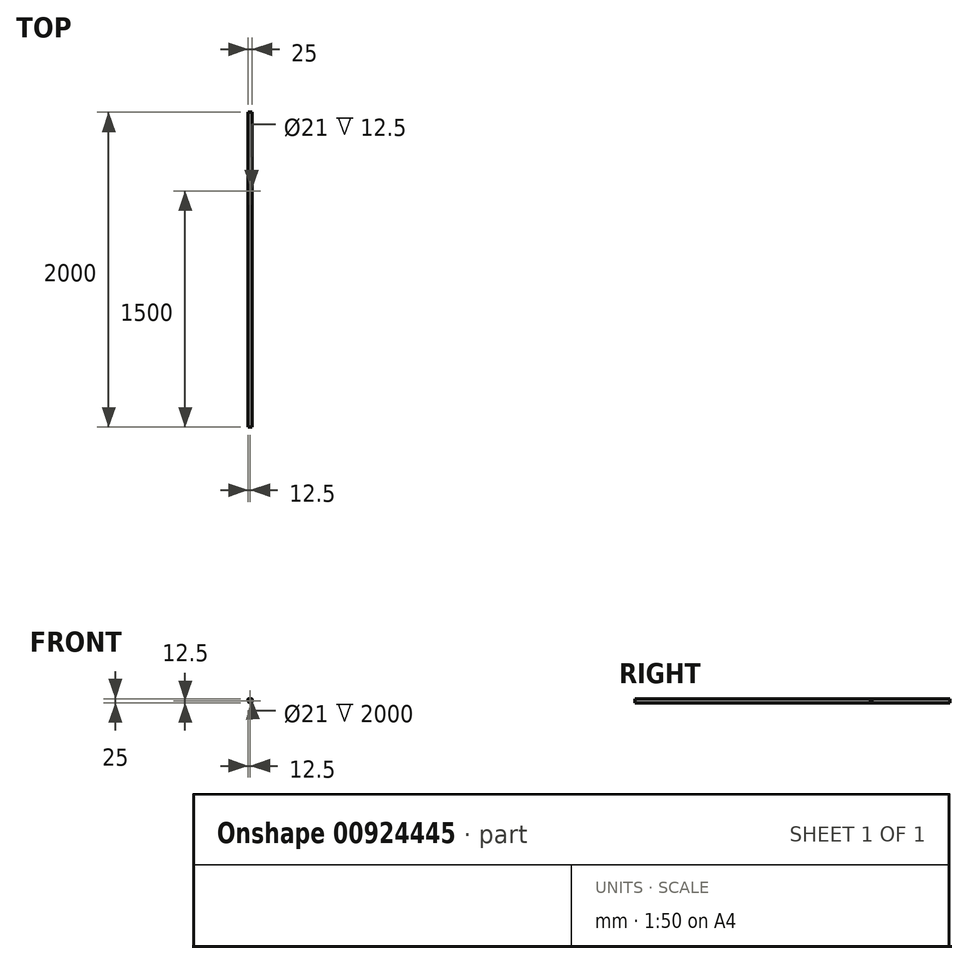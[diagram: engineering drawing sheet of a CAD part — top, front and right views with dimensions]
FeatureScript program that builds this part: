
annotation { "Feature Type Name" : "Feature", "Feature Type Description" : "" }
export const myFeature = defineFeature(function(context is Context, id is Id, definition is map)
    precondition{}
    {
        {
            var Q0;
            Q0=qCreatedBy(makeId("Front.planeOp"),FACE);
            var sketch = newSketch(context, id + "F0", { "sketchPlane" : qUnion([Q0])});
            skCircle(sketch, "E0", {"center": v(0, 0) * mm, "radius": 12.5 * mm});
            skSolve(sketch);
        }
        {
            var Q0;
            Q0=qSketchRegion(id+"F0",true);
            extrude(context, id + "F1", {"entities" : qUnion([Q0]), "depth" : 2000 * mm, "offsetDistance" : 25 * mm});
        }
        {
            var Q0;
            Q0=makeQuery(id+"F1.opExtrude","CAP_FACE",FACE,{"disambiguationData":[OSD([sQuery(id+"F0.wireOp",EDGE,"E0")])],"isStart":false});
            var sketch = newSketch(context, id + "F2", { "sketchPlane" : qUnion([Q0])});
            skCircle(sketch, "E1", {"center": v(0, 0) * mm, "radius": 10.5 * mm});
            skSolve(sketch);
        }
        {
            var Q0;
            Q0=qSketchRegion(id+"F2",true);
            extrude(context, id + "F3", {"entities" : qUnion([Q0]), "operationType" : NewBodyOperationType.REMOVE, "oppositeDirection" : true, "depth" : 2000 * mm, "offsetDistance" : 25 * mm});
        }
        {
            var Q0;
            Q0=qCreatedBy(makeId("Top.planeOp"),FACE);
            var sketch = newSketch(context, id + "F4", { "sketchPlane" : qUnion([Q0])});
            skCircle(sketch, "E2", {"center": v(0, -500) * mm, "radius": 12.5 * mm});
            skSolve(sketch);
        }
        {
            var Q0;
            Q0=qSketchRegion(id+"F4",true);
            extrude(context, id + "F5", {"entities" : qUnion([Q0]), "operationType" : NewBodyOperationType.ADD, "depth" : 12.5 * mm, "offsetDistance" : 25 * mm});
        }
        {
            var Q0;
            Q0=qCreatedBy(makeId("Front.planeOp"),FACE);
            var sketch = newSketch(context, id + "F6", { "sketchPlane" : qUnion([Q0])});
            skCircle(sketch, "E3", {"center": v(0, 0) * mm, "radius": 10.5 * mm});
            skSolve(sketch);
        }
        {
            var Q0;
            Q0=qSketchRegion(id+"F6",true);
            extrude(context, id + "F7", {"entities" : qUnion([Q0]), "operationType" : NewBodyOperationType.REMOVE, "depth" : 1000 * mm, "offsetDistance" : 25 * mm});
        }
        {
            var Q0;
            Q0=makeQuery(id+"F5.opExtrude","CAP_FACE",FACE,{"disambiguationData":[OSD([sQuery(id+"F4.wireOp",EDGE,"E2")])],"isStart":false});
            var sketch = newSketch(context, id + "F8", { "sketchPlane" : qUnion([Q0])});
            skCircle(sketch, "E4", {"center": v(0, -500) * mm, "radius": 10.5 * mm});
            skSolve(sketch);
        }
        {
            var Q0;
            Q0=qSketchRegion(id+"F8",true);
            extrude(context, id + "F9", {"entities" : qUnion([Q0]), "operationType" : NewBodyOperationType.REMOVE, "oppositeDirection" : true, "depth" : 12.5 * mm, "offsetDistance" : 25 * mm});
        }
        {
            var Q0;
            Q0=makeQuery(id+"F5.boolean.opBoolean","INTERSECT",EDGE,{"disambiguationData":[OD(0.0)],"derivedFrom":[makeQuery(id+"F1.opExtrude","SWEPT_FACE",FACE,{"disambiguationData":[OSD([sQuery(id+"F0.wireOp",EDGE,"E0")])]}),makeQuery(id+"F5.opExtrude","SWEPT_FACE",FACE,{"disambiguationData":[OSD([sQuery(id+"F4.wireOp",EDGE,"E2")])]})]});
            var Q1;
            Q1=makeQuery(id+"F5.boolean.opBoolean","INTERSECT",EDGE,{"disambiguationData":[OD(1.0)],"derivedFrom":[makeQuery(id+"F1.opExtrude","SWEPT_FACE",FACE,{"disambiguationData":[OSD([sQuery(id+"F0.wireOp",EDGE,"E0")])]}),makeQuery(id+"F5.opExtrude","SWEPT_FACE",FACE,{"disambiguationData":[OSD([sQuery(id+"F4.wireOp",EDGE,"E2")])]})]});
            fillet(context, id + "F10", {"entities" : qUnion([Q0, Q1]), "radius" : 5 * mm, "tangentPropagation" : true, "allowEdgeOverflow" : false});
        }
    });
